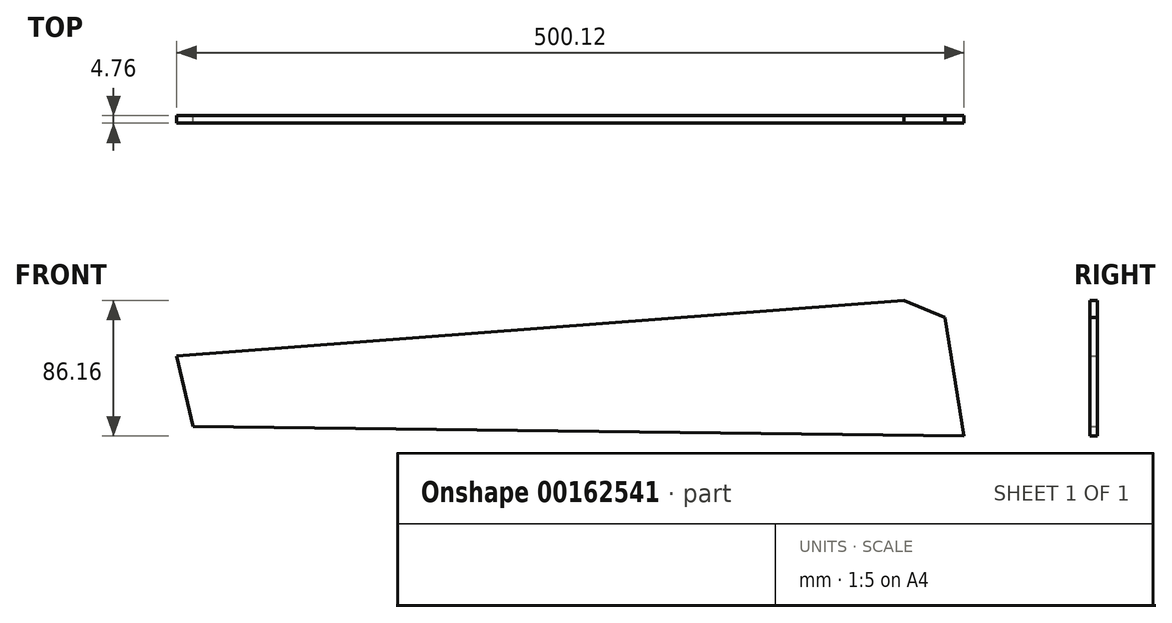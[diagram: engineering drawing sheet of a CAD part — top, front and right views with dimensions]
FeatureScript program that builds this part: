
annotation { "Feature Type Name" : "Feature", "Feature Type Description" : "" }
export const myFeature = defineFeature(function(context is Context, id is Id, definition is map)
    precondition{}
    {
        {
            var Q0;
            Q0=qCreatedBy(makeId("Front.planeOp"),FACE);
            var sketch = newSketch(context, id + "F0", { "sketchPlane" : qUnion([Q0])});
            skLineSegment(sketch, "E0", {"start": v(254.06, 0) * mm, "end": v(241.93, 75.23) * mm});
            skLineSegment(sketch, "E1", {"start": v(219.12, 86.4) * mm, "end": v(-262.07, 49.5) * mm});
            skLineSegment(sketch, "E2", {"start": v(241.93, 75.23) * mm, "end": v(215.95, 86.16) * mm});
            skLineSegment(sketch, "E3", {"start": v(254.06, 0) * mm, "end": v(-252.07, 6.19) * mm});
            skPoint(sketch, "E4.start.orphan", {"position": v(-250.64, 0) * mm});
            skLineSegment(sketch, "E5", {"start": v(-246.06, 50.73) * mm, "end": v(-235.73, 5.99) * mm});
            skSolve(sketch);
        }
        {
            var Q0;
            Q0=qSketchRegion(id+"F0",true);
            extrude(context, id + "F1", {"entities" : qUnion([Q0]), "depth" : 4.76 * mm});
        }
    });
